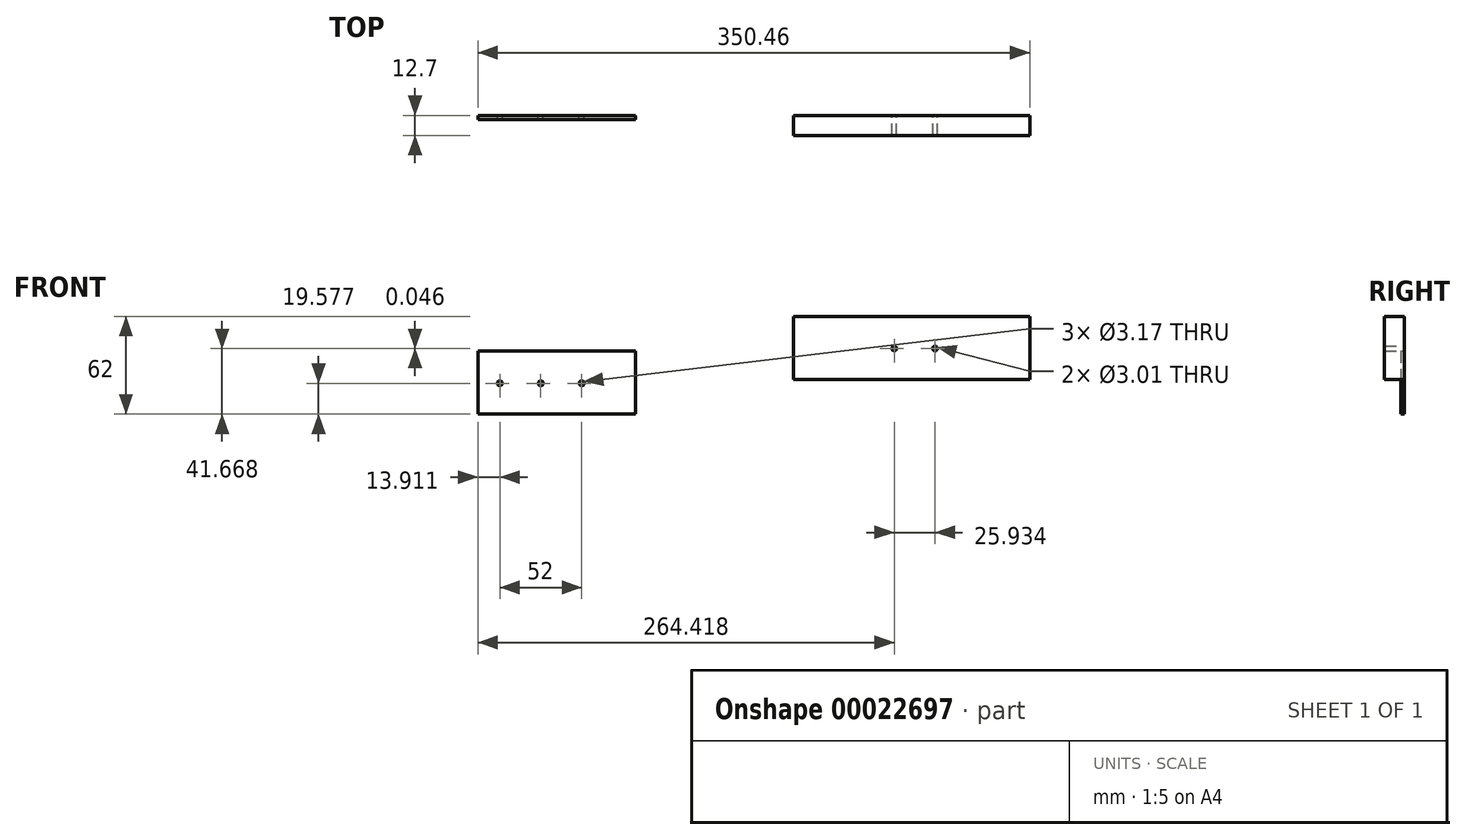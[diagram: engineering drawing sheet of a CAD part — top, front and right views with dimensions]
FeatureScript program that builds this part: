
annotation { "Feature Type Name" : "Feature", "Feature Type Description" : "" }
export const myFeature = defineFeature(function(context is Context, id is Id, definition is map)
    precondition{}
    {
        {
            var Q0;
            Q0=qCreatedBy(makeId("Front.planeOp"),FACE);
            var sketch = newSketch(context, id + "F0", { "sketchPlane" : qUnion([Q0])});
            skLineSegment(sketch, "E0.bottom", {"start": v(-89.41, -5.25) * mm, "end": v(60.59, -5.25) * mm});
            skLineSegment(sketch, "E0.top", {"start": v(-89.41, -45.25) * mm, "end": v(60.59, -45.25) * mm});
            skLineSegment(sketch, "E0.left", {"start": v(-89.41, -5.25) * mm, "end": v(-89.41, -45.25) * mm});
            skLineSegment(sketch, "E0.right", {"start": v(60.59, -5.25) * mm, "end": v(60.59, -45.25) * mm});
            skCircle(sketch, "E1", {"center": v(0.48, -25.58) * mm, "radius": 1.5 * mm});
            skCircle(sketch, "E2", {"center": v(-25.45, -25.54) * mm, "radius": 1.5 * mm});
            skLineSegment(sketch, "E3", {"start": v(-25.45, -25.54) * mm, "end": v(0.55, -25.54) * mm});
            skSolve(sketch);
        }
        {
            var Q0;
            Q0=makeQuery(id+"F0.imprint","IMPRINT",FACE,{"disambiguationData":[TD([[makeQuery(id+"F0.imprint","IMPRINT",EDGE,{"derivedFrom":sQuery(id+"F0.wireOp",EDGE,"E0.bottom")}),-1.0]])]});
            extrude(context, id + "F1", {"entities" : qUnion([Q0]), "depth" : 12.7 * mm});
        }
        {
            var Q0;
            Q0=qCreatedBy(makeId("Front.planeOp"),FACE);
            var sketch = newSketch(context, id + "F2", { "sketchPlane" : qUnion([Q0])});
            skLineSegment(sketch, "E4.bottom", {"start": v(-189.87, -27.25) * mm, "end": v(-289.87, -27.25) * mm});
            skLineSegment(sketch, "E4.top", {"start": v(-189.87, -67.25) * mm, "end": v(-289.87, -67.25) * mm});
            skLineSegment(sketch, "E4.left", {"start": v(-189.87, -27.25) * mm, "end": v(-189.87, -67.25) * mm});
            skLineSegment(sketch, "E4.right", {"start": v(-289.87, -27.25) * mm, "end": v(-289.87, -67.25) * mm});
            skLineSegment(sketch, "E5", {"start": v(-239.87, -27.25) * mm, "end": v(-239.87, -67.25) * mm});
            skCircle(sketch, "E6", {"center": v(-223.96, -47.67) * mm, "radius": 1.59 * mm});
            skCircle(sketch, "E7", {"center": v(-249.96, -47.67) * mm, "radius": 1.59 * mm});
            skCircle(sketch, "E8", {"center": v(-275.96, -47.67) * mm, "radius": 1.59 * mm});
            skLineSegment(sketch, "E9", {"start": v(-223.96, -47.67) * mm, "end": v(-249.96, -47.67) * mm});
            skLineSegment(sketch, "E10", {"start": v(-249.96, -47.67) * mm, "end": v(-275.96, -47.67) * mm});
            skSolve(sketch);
        }
        {
            var Q0;
            Q0=makeQuery(id+"F2.imprint","IMPRINT",FACE,{"disambiguationData":[TD([[makeQuery(id+"F2.imprint","IMPRINT",EDGE,{"derivedFrom":sQuery(id+"F2.wireOp",EDGE,"E4.bottom")}),1.0]])]});
            var Q1;
            {var subQ4=sQuery(id+"F2.wireOp",EDGE,"E4.right");Q1=makeQuery(id+"F2.imprint","IMPRINT",FACE,{"disambiguationData":[TD([[makeQuery(id+"F2.imprint","IMPRINT",EDGE,{"derivedFrom":subQ4}),1.0]])]});}
            extrude(context, id + "F3", {"entities" : qUnion([Q0, Q1]), "depth" : 2.5 * mm});
        }
    });
